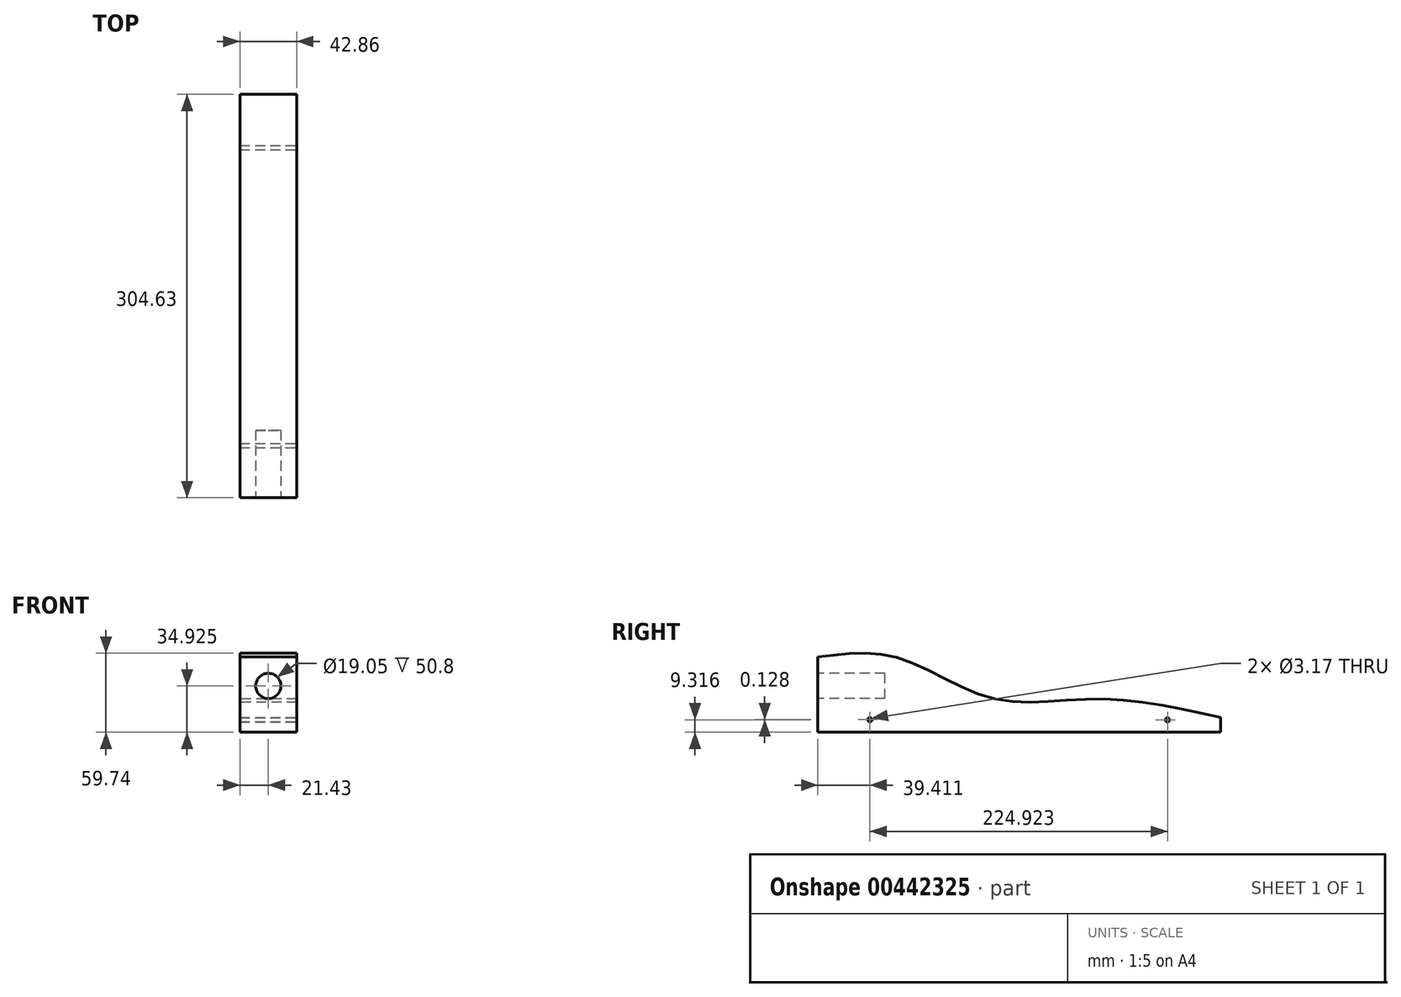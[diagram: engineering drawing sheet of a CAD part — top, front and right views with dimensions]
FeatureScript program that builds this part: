
annotation { "Feature Type Name" : "Feature", "Feature Type Description" : "" }
export const myFeature = defineFeature(function(context is Context, id is Id, definition is map)
    precondition{}
    {
        {
            var Q0;
            Q0=qCreatedBy(makeId("Right.planeOp"),FACE);
            var sketch = newSketch(context, id + "F0", { "sketchPlane" : qUnion([Q0])});
            skLineSegment(sketch, "E0", {"start": v(-152.4, 0) * mm, "end": v(152.4, 0) * mm});
            skLineSegment(sketch, "E1", {"start": v(-152.4, 0) * mm, "end": v(-152.4, 69.85) * mm});
            skLineSegment(sketch, "E2", {"start": v(152.4, 0) * mm, "end": v(152.4, 19.05) * mm});
            skLineSegment(sketch, "E3", {"start": v(152.4, 19.05) * mm, "end": v(-152.4, 69.85) * mm});
            skPoint(sketch, "E4.endSnap0", {"position": v(-152.4, 34.93) * mm});
            skLineSegment(sketch, "E5.0", {"start": v(-95.25, 50.8) * mm, "end": v(-152.4, 50.8) * mm, "construction": true});
            skLineSegment(sketch, "E5.1", {"start": v(-95.25, 50.8) * mm, "end": v(-95.25, 19.05) * mm, "construction": true});
            skLineSegment(sketch, "E5.2", {"start": v(-95.25, 19.05) * mm, "end": v(-152.4, 19.05) * mm, "construction": true});
            skSolve(sketch);
        }
        {
            var Q0;
            Q0=makeQuery(id+"F0.imprint","IMPRINT",FACE,{"disambiguationData":[TD([[makeQuery(id+"F0.imprint","IMPRINT",EDGE,{"derivedFrom":sQuery(id+"F0.wireOp",EDGE,"E0")}),1.0]])]});
            extrude(context, id + "F1", {"entities" : qUnion([Q0]), "depth" : 42.86 * mm, "symmetric" : true});
        }
        {
            var Q0;
            Q0=makeQuery(id+"F1.opExtrude","SWEPT_FACE",FACE,{"disambiguationData":[OSD([sQuery(id+"F0.wireOp",EDGE,"E1")])]});
            var sketch = newSketch(context, id + "F2", { "sketchPlane" : qUnion([Q0])});
            skLineSegment(sketch, "E6", {"start": v(21.43, 34.93) * mm, "end": v(0, 34.93) * mm, "construction": true});
            skCircle(sketch, "E7", {"center": v(0, 34.93) * mm, "radius": 9.53 * mm});
            skSolve(sketch);
        }
        {
            var Q0;
            Q0=makeQuery(id+"F2.imprint","IMPRINT",FACE,{"disambiguationData":[TD([[makeQuery(id+"F2.imprint","IMPRINT",EDGE,{"derivedFrom":sQuery(id+"F2.wireOp",EDGE,"E7")}),1.0]])]});
            var Q1;
            Q1=sQuery(id+"F2.wireOp",EDGE,"E7");
            extrude(context, id + "F3", {"entities" : qUnion([Q0]), "operationType" : NewBodyOperationType.REMOVE, "surfaceEntities" : qUnion([Q1]), "oppositeDirection" : true, "depth" : 50.8 * mm});
        }
        {
            var Q0;
            Q0=makeQuery(id+"F1.opExtrude","CAP_FACE",FACE,{"disambiguationData":[OSD([sQuery(id+"F0.wireOp",EDGE,"E0"),sQuery(id+"F0.wireOp",EDGE,"E1"),sQuery(id+"F0.wireOp",EDGE,"E2"),sQuery(id+"F0.wireOp",EDGE,"E3")])],"isStart":false});
            var sketch = newSketch(context, id + "F4", { "sketchPlane" : qUnion([Q0])});
            skLineSegment(sketch, "E8", {"start": v(-152.4, 34.93) * mm, "end": v(-152.4, 44.45) * mm, "construction": true});
            skLineSegment(sketch, "E9.0", {"start": v(-95.25, 19.05) * mm, "end": v(-152.4, 19.05) * mm, "construction": true});
            skLineSegment(sketch, "E9.1", {"start": v(-95.25, 50.8) * mm, "end": v(-95.25, 19.05) * mm, "construction": true});
            skLineSegment(sketch, "E9.2", {"start": v(-152.4, 50.8) * mm, "end": v(-95.25, 50.8) * mm, "construction": true});
            skLineSegment(sketch, "E10", {"start": v(57.15, 0) * mm, "end": v(57.15, 34.93) * mm, "construction": true});
            skLineSegment(sketch, "E11", {"start": v(-152.4, 44.45) * mm, "end": v(-101.6, 44.45) * mm, "construction": true});
            skLineSegment(sketch, "E12", {"start": v(-101.6, 44.45) * mm, "end": v(-101.6, 25.4) * mm, "construction": true});
            skLineSegment(sketch, "E13", {"start": v(-101.6, 25.4) * mm, "end": v(-152.4, 25.4) * mm, "construction": true});
            skSolve(sketch);
        }
        {
            var Q0;
            Q0=makeQuery(id+"F4.imprint","IMPRINT",FACE,{"disambiguationData":[TD([[makeQuery(id+"F4.imprint","IMPRINT",EDGE,{"derivedFrom":makeQuery(id+"F1.opExtrude","CAP_EDGE",EDGE,{"disambiguationData":[OSD([sQuery(id+"F0.wireOp",EDGE,"E0")])],"isStart":false})}),1.0]])]});
            var sketch = newSketch(context, id + "F5", { "sketchPlane" : qUnion([Q0])});
            skFitSpline(sketch, "E14", {"points": [v(-152.66, 56.73) * mm, v(-91.64, 56.16) * mm, v(-20.84, 25.65) * mm, v(59.17, 25.07) * mm, v(152.23, 11.26) * mm], "startDerivative": vector(274.54, 36.5) * mm, "endDerivative": vector(341.17, -74.99) * mm});
            skLineSegment(sketch, "E15", {"start": v(152.23, 11.26) * mm, "end": v(152.23, 0) * mm});
            skFitSpline(sketch, "E16", {"points": [v(152.23, 0) * mm, v(-152.48, 0) * mm], "startDerivative": vector(-304.36, -2.02) * mm, "endDerivative": vector(-304.53, 0.52) * mm});
            skLineSegment(sketch, "E17", {"start": v(-152.66, 56.73) * mm, "end": v(-152.48, 0) * mm});
            skLineSegment(sketch, "E18", {"start": v(-112.99, -0.08) * mm, "end": v(-112.99, 9.44) * mm, "construction": true});
            skCircle(sketch, "E19", {"center": v(-112.99, 9.44) * mm, "radius": 1.59 * mm});
            skLineSegment(sketch, "E20", {"start": v(111.93, -0.2) * mm, "end": v(111.93, 9.32) * mm, "construction": true});
            skCircle(sketch, "E21", {"center": v(111.93, 9.32) * mm, "radius": 1.59 * mm});
            skSolve(sketch);
        }
        {
            var Q0;
            Q0 = qSketchRegion(id + "F5", true);
            extrude(context, id + "F6", {"entities" : qUnion([Q0]), "operationType" : NewBodyOperationType.INTERSECT, "endBound" : BoundingType.THROUGH_ALL, "oppositeDirection" : true, "depth" : 25.4 * mm});
        }
    });
